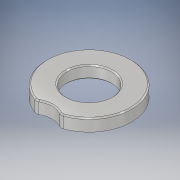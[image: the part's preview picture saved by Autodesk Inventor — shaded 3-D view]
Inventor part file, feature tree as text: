
AUTODESK INVENTOR PART (.ipt)
format: ipt  version: 2019.3 (Build 233278000, 278)  size: 162,816 bytes
history: native  units: mm
features: chamfer x2, extrude x1, fillet x1, sketch x1
ambient origin geometry x8: Origin, YZ Plane, XZ Plane, XY Plane, X Axis, Y Axis, Z Axis, Center Point
bodies: Solid1 (feature_tree)
feature tree (5):
  extrude  "Extrusion1"  Depth=10.0mm
  fillet  "Fillet1"  Radius=40.0mm
  chamfer  "Chamfer1"  Angle=45.0deg  [1 undecoded]
  chamfer  "Chamfer2"  Distance=20.0mm
  sketch  "Sketch1"  dims[d0=18.5mm d2=3.4mm d4=40.0mm d6=360.0deg d8=45.0deg d10=20.0mm d11=10.0mm d12=5.0mm d13=0.0mm d14=2.0mm d24=0.5mm d25=2.0mm d26=45.0deg d30=7.5mm d31=3.75mm d32=0.5mm d33=2.0mm d34=45.0deg]
note: 1 required parameter value undecoded (feature->parameter linkage not recoverable at this tier; creation-order binding heuristic only, values carry confidence <= 0.55)
